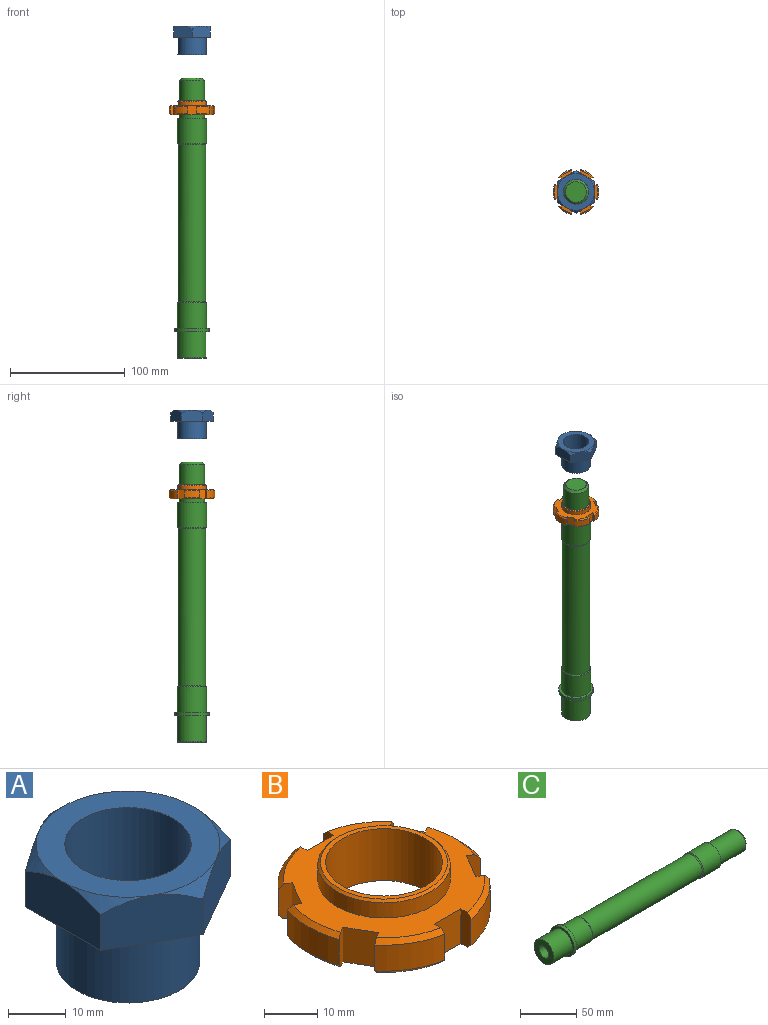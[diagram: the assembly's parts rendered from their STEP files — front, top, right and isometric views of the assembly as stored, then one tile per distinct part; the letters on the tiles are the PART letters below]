
ASSEMBLY  parts=3 mates=2
PART A: 17 faces, bbox 37x37x25 mm
  f0: plane 32x32mm, normal (0,0,1), area 424.1mm2, adj f7,f11,f12,f13,f14,f15,f16
  f1: plane 16x10.01mm, normal (0.5,0.87,0), area 169.1mm2, adj f2,f6,f10,f11,f16
  f2: plane 18.5x10.01mm, normal (1,0,0), area 169.1mm2, adj f1,f3,f10,f15,f16
  f3: plane 16x10.01mm, normal (0.5,-0.87,0), area 169.1mm2, adj f2,f4,f10,f14,f15
  f4: plane 16x10.01mm, normal (-0.5,-0.87,0), area 169.1mm2, adj f3,f5,f10,f13,f14
  f5: plane 18.5x10.01mm, normal (-1,0,0), area 169.1mm2, adj f4,f6,f10,f12,f13
  f6: plane 16x10.01mm, normal (-0.5,0.87,0), area 169.1mm2, adj f1,f5,f10,f11,f12
  f7: cylinder r=11mm len=25mm, axis (0,0,-1), area 1727.9mm2, adj f0,f9
  f8: cylinder r=12.5mm len=25mm, axis (0,0,-1), area 1178.1mm2, adj f9,f10
  f9: plane 25x25mm, normal (0,0,-1), area 110.7mm2, adj f7,f8
  f10: plane 36.95x32mm, normal (0,0,-1), area 395.9mm2, adj f1,f2,f3,f4,f5,f6,f8
  f11: cone r=22.86mm half-angle=45deg, axis (0,0,-1), area 19.5mm2, adj f0,f1,f6
  f12: cone r=22.86mm half-angle=45deg, axis (0,0,-1), area 19.5mm2, adj f0,f5,f6
  f13: cone r=22.86mm half-angle=45deg, axis (0,0,-1), area 19.5mm2, adj f0,f4,f5
  f14: cone r=22.86mm half-angle=45deg, axis (0,0,-1), area 19.5mm2, adj f0,f3,f4
  f15: cone r=22.86mm half-angle=45deg, axis (0,0,-1), area 19.5mm2, adj f0,f2,f3
  f16: cone r=22.86mm half-angle=45deg, axis (0,0,-1), area 19.5mm2, adj f0,f1,f2
PART B: 42 faces, bbox 40x39.4x12 mm
  f0: cylinder r=20mm len=11.8mm, axis (0,0,-1), area 83.4mm2, adj f7,f12,f37,f40
  f1: cylinder r=20mm len=13.63mm, axis (0,0,-1), area 83.4mm2, adj f8,f13,f34,f38
  f2: cylinder r=20mm len=11.8mm, axis (0,0,-1), area 83.4mm2, adj f9,f14,f31,f35
  f3: cylinder r=20mm len=11.8mm, axis (0,0,-1), area 83.4mm2, adj f10,f15,f28,f32
  f4: cylinder r=20mm len=13.63mm, axis (0,0,-1), area 83.4mm2, adj f11,f16,f25,f29
  f5: plane 38x37.35mm, normal (0,0,1), area 563.8mm2, adj f12,f13,f14,f15,f16,f18,f23,f24
  f6: plane 38x37.35mm, normal (0,0,-1), area 674.5mm2, adj f7,f8,f9,f10,f11,f20,f22,f24
  f7: cone r=20mm half-angle=45deg, axis (0,0,1), area 18.9mm2, adj f0,f6,f37,f40
  f8: cone r=20mm half-angle=45deg, axis (0,0,1), area 18.9mm2, adj f1,f6,f34,f38
  f9: cone r=20mm half-angle=45deg, axis (0,0,1), area 18.9mm2, adj f2,f6,f31,f35
  f10: cone r=20mm half-angle=45deg, axis (0,0,1), area 18.9mm2, adj f3,f6,f28,f32
  f11: cone r=20mm half-angle=45deg, axis (0,0,1), area 18.9mm2, adj f4,f6,f25,f29
  f12: cone r=19mm half-angle=45deg, axis (0,0,-1), area 18.9mm2, adj f0,f5,f37,f40
  f13: cone r=19mm half-angle=45deg, axis (0,0,-1), area 18.9mm2, adj f1,f5,f34,f38
  f14: cone r=19mm half-angle=45deg, axis (0,0,-1), area 18.9mm2, adj f2,f5,f31,f35
  f15: cone r=19mm half-angle=45deg, axis (0,0,-1), area 18.9mm2, adj f3,f5,f28,f32
  f16: cone r=19mm half-angle=45deg, axis (0,0,-1), area 18.9mm2, adj f4,f5,f25,f29
  f17: cylinder r=20mm len=11.8mm, axis (0,0,-1), area 83.4mm2, adj f22,f23,f26,f41
  f18: cylinder r=12.5mm len=25mm, axis (0,0,-1), area 274.9mm2, adj f5,f21
  f19: plane 24x24mm, normal (0,0,1), area 72.3mm2, adj f20,f21
  f20: cylinder r=11mm len=22mm, axis (0,0,1), area 829.4mm2, adj f6,f19
  f21: cone r=12mm half-angle=45deg, axis (0,0,-1), area 54.4mm2, adj f18,f19
  f22: cone r=20mm half-angle=45deg, axis (0,0,1), area 18.9mm2, adj f6,f17,f26,f41
  f23: cone r=19mm half-angle=45deg, axis (0,0,-1), area 18.9mm2, adj f5,f17,f26,f41
  f24: plane 8x6.06mm, normal (-0.87,-0.5,0), area 56mm2, adj f5,f6,f25,f26
  f25: plane 8x2.34mm, normal (0.5,-0.87,0), area 20.5mm2, adj f4,f5,f6,f11,f16,f24
  f26: plane 8x2.34mm, normal (-0.5,0.87,0), area 20.5mm2, adj f5,f6,f17,f22,f23,f24
  f27: plane 8x6.06mm, normal (-0.87,0.5,0), area 56mm2, adj f5,f6,f28,f29
  f28: plane 8x2.34mm, normal (-0.5,-0.87,0), area 20.5mm2, adj f3,f5,f6,f10,f15,f27
  f29: plane 8x2.34mm, normal (0.5,0.87,0), area 20.5mm2, adj f4,f5,f6,f11,f16,f27
  f30: plane 8x7mm, normal (0,1,0), area 56mm2, adj f5,f6,f31,f32
  f31: plane 8x2.7mm, normal (-1,0,0), area 20.5mm2, adj f2,f5,f6,f9,f14,f30
  f32: plane 8x2.7mm, normal (1,0,0), area 20.5mm2, adj f3,f5,f6,f10,f15,f30
  f33: plane 8x6.06mm, normal (0.87,0.5,0), area 56mm2, adj f5,f6,f34,f35
  f34: plane 8x2.34mm, normal (-0.5,0.87,0), area 20.5mm2, adj f1,f5,f6,f8,f13,f33
  f35: plane 8x2.34mm, normal (0.5,-0.87,0), area 20.5mm2, adj f2,f5,f6,f9,f14,f33
  f36: plane 8x6.06mm, normal (0.87,-0.5,0), area 56mm2, adj f5,f6,f37,f38
  f37: plane 8x2.34mm, normal (0.5,0.87,0), area 20.5mm2, adj f0,f5,f6,f7,f12,f36
  f38: plane 8x2.34mm, normal (-0.5,-0.87,0), area 20.5mm2, adj f1,f5,f6,f8,f13,f36
  f39: plane 8x7mm, normal (0,-1,0), area 56mm2, adj f5,f6,f40,f41
  f40: plane 8x2.7mm, normal (-1,0,0), area 20.5mm2, adj f0,f5,f6,f7,f12,f39
  f41: plane 8x2.7mm, normal (1,0,0), area 20.5mm2, adj f5,f6,f17,f22,f23,f39
PART C: 20 faces, bbox 244x32.5x32.5 mm
  f0: cylinder r=12.5mm len=25mm, axis (-1,0,0), area 1798.6mm2, adj f4,f18
  f1: plane 24.8x24.8mm, normal (-1,0,0), area 366.2mm2, adj f17,f18
  f2: cylinder r=15mm len=30mm, axis (-1,0,0), area 263.9mm2, adj f15,f16
  f3: plane 29.8x29.8mm, normal (1,0,0), area 190.8mm2, adj f5,f16
  f4: plane 29.8x29.8mm, normal (-1,0,0), area 206.6mm2, adj f0,f15
  f5: cylinder r=12.7mm len=25.4mm, axis (-1,0,0), area 1755.5mm2, adj f3,f13
  f6: cylinder r=12mm len=137.09mm, axis (-1,0,0), area 10336.5mm2, adj f13,f14
  f7: cylinder r=12.7mm len=25.4mm, axis (-1,0,0), area 1755.5mm2, adj f8,f14
  f8: plane 25.4x25.4mm, normal (1,0,0), area 126.6mm2, adj f7,f9
  f9: cylinder r=11mm len=33mm, axis (-1,0,0), area 2280.8mm2, adj f8,f19
  f10: plane 18x18mm, normal (1,0,0), area 254.5mm2, adj f19
  f11: cone r=0mm half-angle=59deg, axis (-1,0,0), area 131.9mm2, adj f12
  f12: cylinder r=6mm len=34.9mm, axis (-1,0,0), area 1315.7mm2, adj f11,f17
  f13: torus R=13mm, axis (-1,0,0), area 97.4mm2, adj f5,f6
  f14: torus R=13mm, axis (1,0,0), area 97.4mm2, adj f6,f7
  f15: torus R=14.9mm, axis (1,0,0), area 14.8mm2, adj f2,f4
  f16: torus R=14.9mm, axis (1,0,0), area 14.8mm2, adj f2,f3
  f17: torus R=6.1mm, axis (1,0,0), area 6mm2, adj f1,f12
  f18: torus R=12.4mm, axis (1,0,0), area 12.3mm2, adj f0,f1
  f19: cone r=9mm half-angle=45deg, axis (-1,0,0), area 177.7mm2, adj f9,f10
PLACE A t=(218.15,113.46,-38.61)mm
PLACE B t=(218.15,113.46,-90.94)mm
PLACE C rot(axis=(0.71,0,0.71),180deg) t=(218.15,113.46,-303.08)mm
MATE slider C.f9 <-> B.f20  axis (0,0,1) through (218.15,113.46,-59.08)mm
MATE slider C.f9 <-> A.f7  axis (0,0,1) through (218.15,113.46,-59.08)mm
